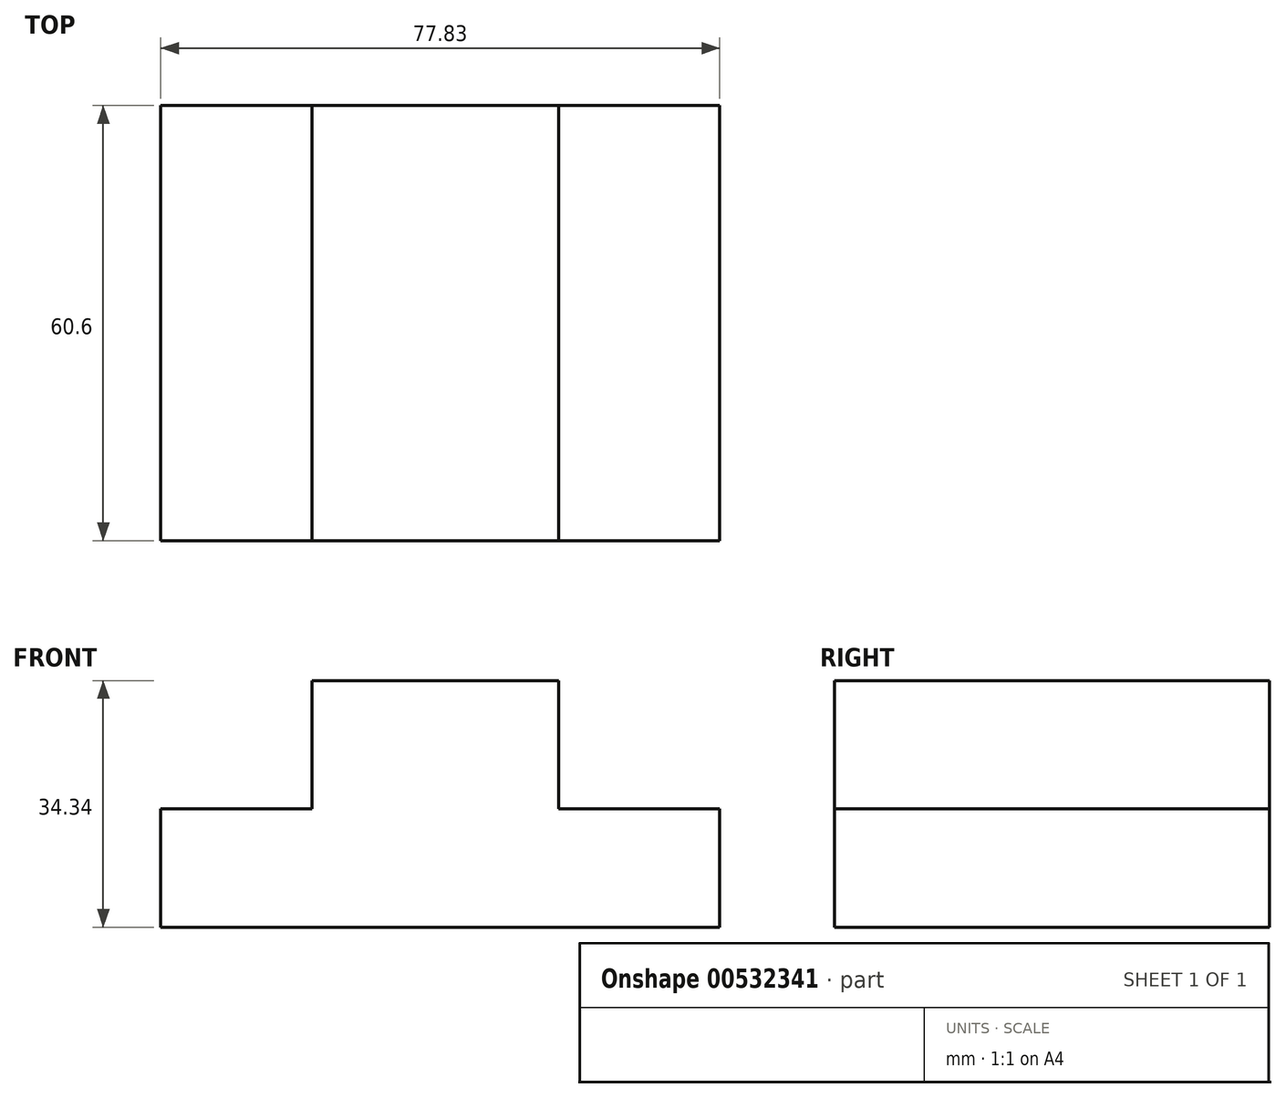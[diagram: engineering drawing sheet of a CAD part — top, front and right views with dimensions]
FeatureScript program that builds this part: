
annotation { "Feature Type Name" : "Feature", "Feature Type Description" : "" }
export const myFeature = defineFeature(function(context is Context, id is Id, definition is map)
    precondition{}
    {
        {
            var Q0;
            Q0=qCreatedBy(makeId("Front.planeOp"),FACE);
            var sketch = newSketch(context, id + "F0", { "sketchPlane" : qUnion([Q0])});
            skLineSegment(sketch, "E0", {"start": v(-37.77, 0) * mm, "end": v(40.06, 0) * mm});
            skLineSegment(sketch, "E1", {"start": v(40.06, 0) * mm, "end": v(40.06, 16.48) * mm});
            skLineSegment(sketch, "E2", {"start": v(40.06, 16.48) * mm, "end": v(17.63, 16.48) * mm});
            skLineSegment(sketch, "E3", {"start": v(17.63, 16.48) * mm, "end": v(17.63, 34.34) * mm});
            skLineSegment(sketch, "E4", {"start": v(17.63, 34.34) * mm, "end": v(-16.71, 34.34) * mm});
            skLineSegment(sketch, "E5", {"start": v(-16.71, 34.34) * mm, "end": v(-16.71, 16.48) * mm});
            skLineSegment(sketch, "E6", {"start": v(-16.71, 16.48) * mm, "end": v(-37.77, 16.48) * mm});
            skLineSegment(sketch, "E7", {"start": v(-37.77, 16.48) * mm, "end": v(-37.77, 0) * mm});
            skSolve(sketch);
        }
        {
            var Q0;
            Q0=makeQuery(id+"F0.imprint","IMPRINT",FACE,{"disambiguationData":[TD([[makeQuery(id+"F0.imprint","IMPRINT",EDGE,{"derivedFrom":sQuery(id+"F0.wireOp",EDGE,"E0")}),1.0]])]});
            extrude(context, id + "F1", {"entities" : qUnion([Q0]), "endBound" : BoundingType.SYMMETRIC, "depth" : 60.6 * mm, "offsetDistance" : 25 * mm});
        }
    });
